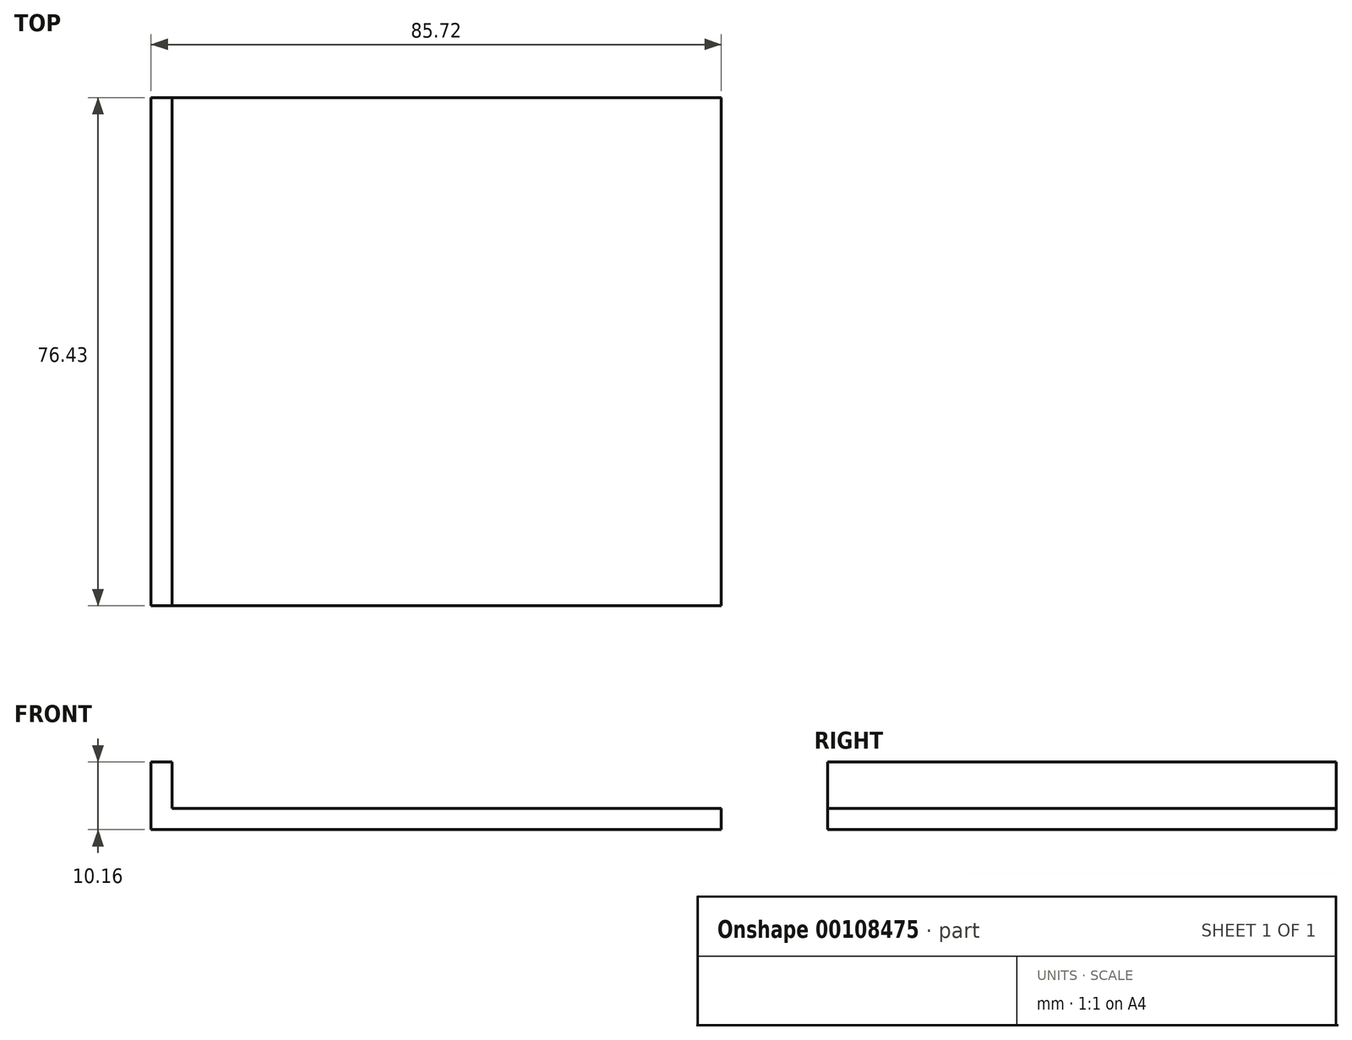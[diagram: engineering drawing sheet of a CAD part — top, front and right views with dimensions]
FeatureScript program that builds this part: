
annotation { "Feature Type Name" : "Feature", "Feature Type Description" : "" }
export const myFeature = defineFeature(function(context is Context, id is Id, definition is map)
    precondition{}
    {
        {
            var Q0;
            Q0=qCreatedBy(makeId("Front.planeOp"),FACE);
            var sketch = newSketch(context, id + "F0", { "sketchPlane" : qUnion([Q0])});
            skLineSegment(sketch, "E0", {"start": v(0, 0) * mm, "end": v(0, 10.16) * mm});
            skLineSegment(sketch, "E1", {"start": v(0, 0) * mm, "end": v(85.73, 0) * mm});
            skLineSegment(sketch, "E2", {"start": v(85.73, 0) * mm, "end": v(85.73, 3.18) * mm});
            skLineSegment(sketch, "E3", {"start": v(0, 10.16) * mm, "end": v(3.17, 10.16) * mm});
            skLineSegment(sketch, "E4", {"start": v(85.73, 3.18) * mm, "end": v(3.17, 3.18) * mm});
            skLineSegment(sketch, "E5", {"start": v(3.17, 10.16) * mm, "end": v(3.17, 3.18) * mm});
            skSolve(sketch);
        }
        {
            var Q0;
            Q0=makeQuery(id+"F0.imprint","IMPRINT",FACE,{"disambiguationData":[TD([[makeQuery(id+"F0.imprint","IMPRINT",EDGE,{"derivedFrom":sQuery(id+"F0.wireOp",EDGE,"E0")}),-1.0]])]});
            extrude(context, id + "F1", {"entities" : qUnion([Q0]), "depth" : 76.43 * mm});
        }
    });
